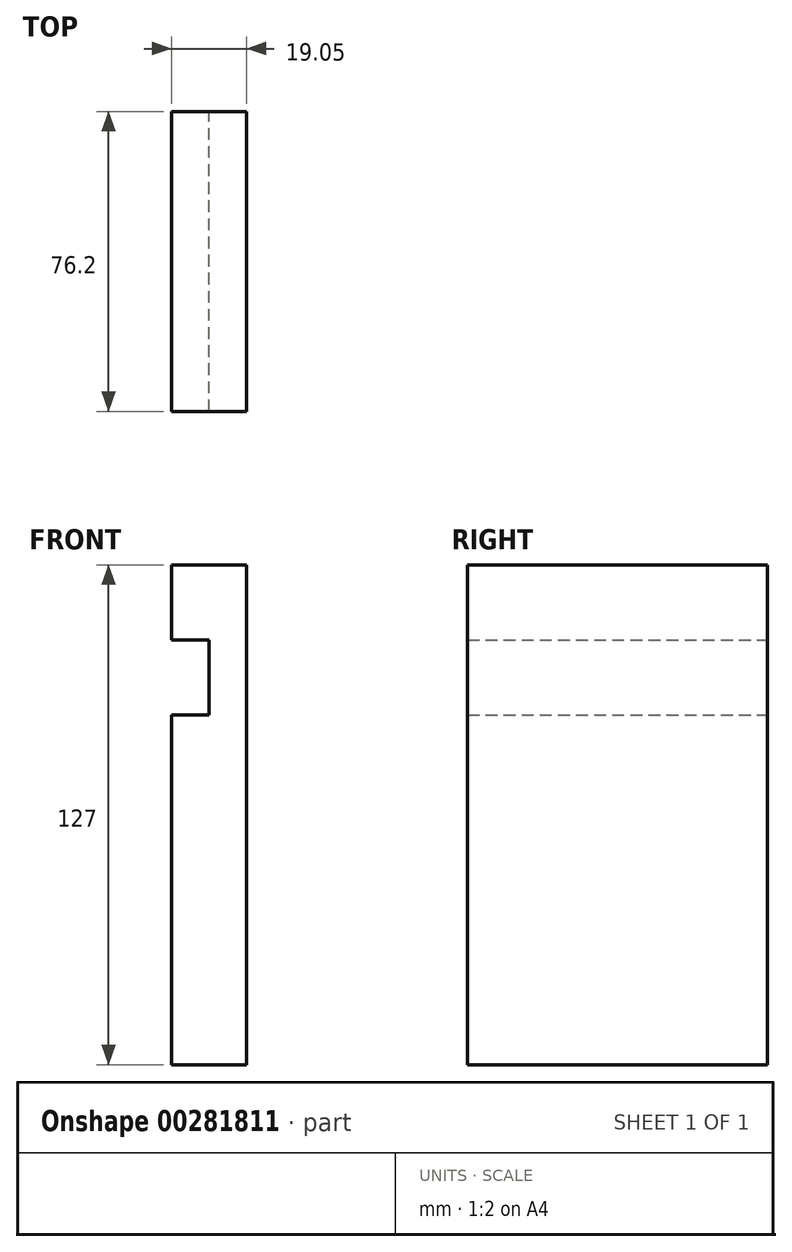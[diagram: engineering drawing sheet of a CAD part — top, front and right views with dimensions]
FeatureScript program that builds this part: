
annotation { "Feature Type Name" : "Feature", "Feature Type Description" : "" }
export const myFeature = defineFeature(function(context is Context, id is Id, definition is map)
    precondition{}
    {
        {
            var Q0;
            Q0=qCreatedBy(makeId("Front.planeOp"),FACE);
            var sketch = newSketch(context, id + "F0", { "sketchPlane" : qUnion([Q0])});
            skLineSegment(sketch, "E0", {"start": v(0, 0) * mm, "end": v(0, 127) * mm});
            skLineSegment(sketch, "E1", {"start": v(0, 127) * mm, "end": v(-19.05, 127) * mm});
            skLineSegment(sketch, "E2", {"start": v(-19.05, 127) * mm, "end": v(-19.05, 107.95) * mm});
            skLineSegment(sketch, "E3", {"start": v(-19.05, 107.95) * mm, "end": v(-9.52, 107.95) * mm});
            skLineSegment(sketch, "E4", {"start": v(-9.52, 107.95) * mm, "end": v(-9.52, 88.9) * mm});
            skLineSegment(sketch, "E5", {"start": v(-9.52, 88.9) * mm, "end": v(-19.05, 88.9) * mm});
            skLineSegment(sketch, "E6", {"start": v(-19.05, 88.9) * mm, "end": v(-19.05, 0) * mm});
            skLineSegment(sketch, "E7", {"start": v(-19.05, 0) * mm, "end": v(0, 0) * mm});
            skSolve(sketch);
        }
        {
            var Q0;
            Q0 = qSketchRegion(id + "F0", true);
            extrude(context, id + "F1", {"entities" : qUnion([Q0]), "depth" : 76.2 * mm});
        }
    });
